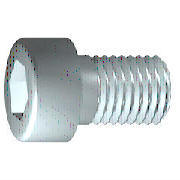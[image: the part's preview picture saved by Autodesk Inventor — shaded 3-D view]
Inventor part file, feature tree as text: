
AUTODESK INVENTOR PART (.ipt)
format: ipt  version: 2015 (Build 190159000, 159)  size: 190,464 bytes
history: native  units: mm (DEFAULTED — no unit token found)
features: sketch x2, extrude x1, plane x1, fillet x1
ambient origin geometry x7: Origin, YZ Plane, XY Plane, X Axis, Y Axis, Z Axis, Center Point
bodies: Solid1 (feature_tree), Body (feature_tree)
feature tree (5):
  extrude  "Slot"  Depth=2.0mm
  plane  "Work Plane1"
  fillet  "Fillet2"  Radius=2.0mm
  sketch  "Sketch1"  dims[d1=15.0mm d2=0.24548mm d3=2.0mm]
  sketch  "Sketch2"  dims[d4=1.0mm d5=60.0deg d6=2.0mm d7=2.0mm d8=1.732051mm d9=3.8mm d10=90.0deg d11=10.0mm d12=0.0mm d13=15.0mm d14=0.0mm d15=0.24538mm d16=0.24538mm d17=0.2mm d19=0.0mm d26=16.0mm d27=45.0deg d28=0.0mm d29=0.0mm d30=0.1mm]
